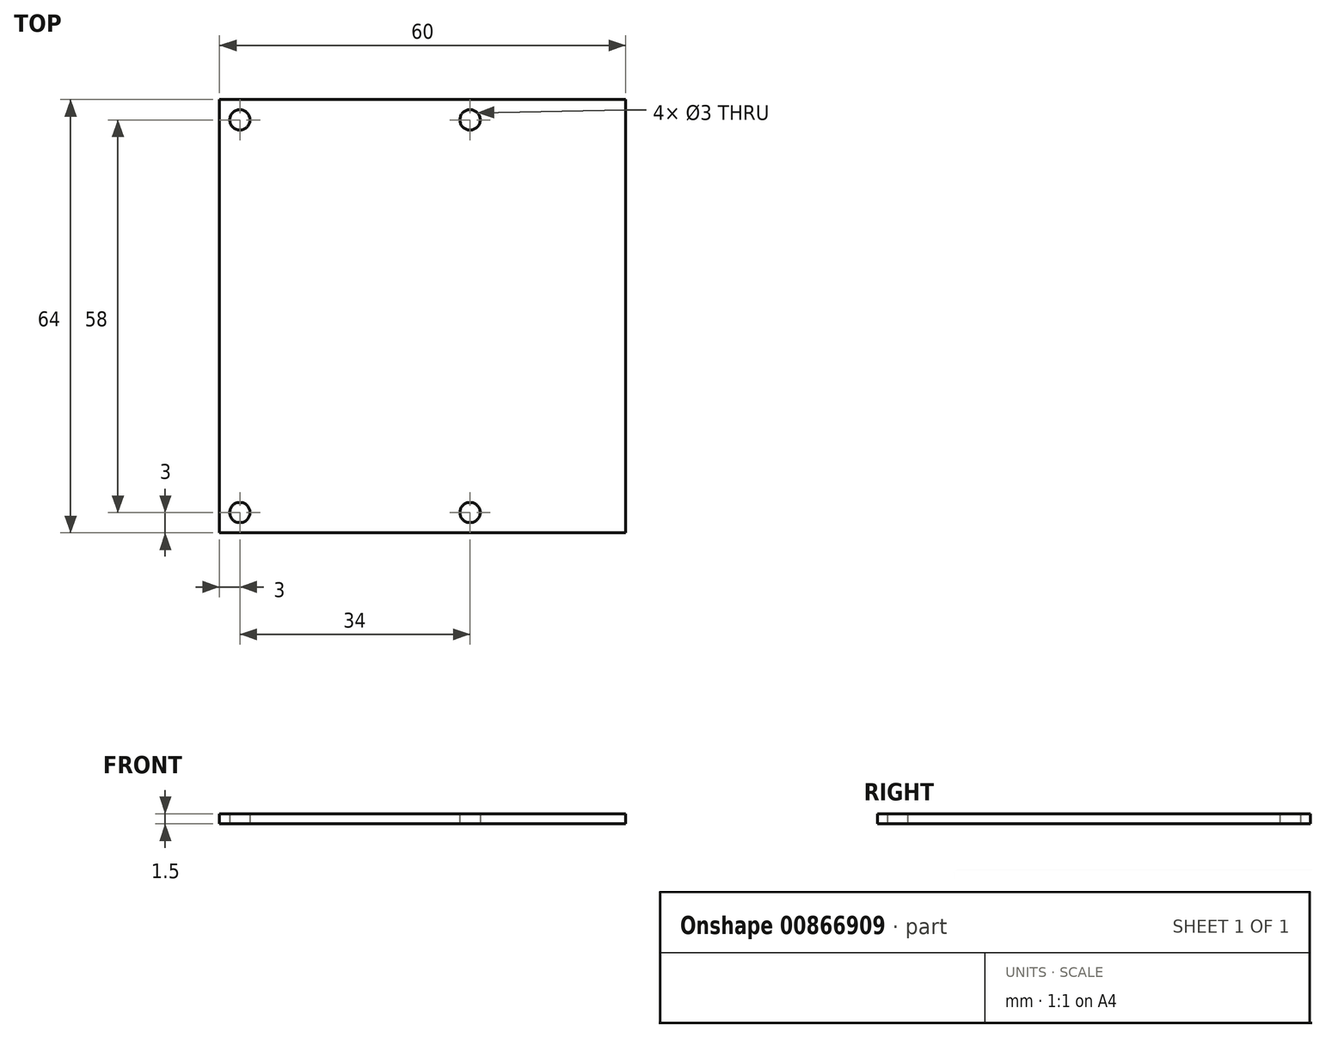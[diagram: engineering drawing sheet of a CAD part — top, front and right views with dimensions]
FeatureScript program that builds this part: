
annotation { "Feature Type Name" : "Feature", "Feature Type Description" : "" }
export const myFeature = defineFeature(function(context is Context, id is Id, definition is map)
    precondition{}
    {
        {
            var Q0;
            Q0=qCreatedBy(makeId("Top.planeOp"),FACE);
            var sketch = newSketch(context, id + "F0", { "sketchPlane" : qUnion([Q0])});
            skLineSegment(sketch, "E0.bottom", {"start": v(30, -32) * mm, "end": v(-30, -32) * mm});
            skLineSegment(sketch, "E0.top", {"start": v(30, 32) * mm, "end": v(-30, 32) * mm});
            skLineSegment(sketch, "E0.left", {"start": v(30, -32) * mm, "end": v(30, 32) * mm});
            skLineSegment(sketch, "E0.right", {"start": v(-30, -32) * mm, "end": v(-30, 32) * mm});
            skPoint(sketch, "E1.middle", {"position": v(0, 0) * mm});
            skCircle(sketch, "E2", {"center": v(7, 29) * mm, "radius": 1.5 * mm});
            skCircle(sketch, "E3", {"center": v(7, -29) * mm, "radius": 1.5 * mm});
            skCircle(sketch, "E4", {"center": v(-27, -29) * mm, "radius": 1.5 * mm});
            skCircle(sketch, "E5", {"center": v(-27, 29) * mm, "radius": 1.5 * mm});
            skLineSegment(sketch, "E6.bottom", {"start": v(7, -29) * mm, "end": v(-27, -29) * mm, "construction": true});
            skLineSegment(sketch, "E6.top", {"start": v(7, 29) * mm, "end": v(-27, 29) * mm, "construction": true});
            skLineSegment(sketch, "E6.left", {"start": v(7, -29) * mm, "end": v(7, 29) * mm, "construction": true});
            skLineSegment(sketch, "E6.right", {"start": v(-27, -29) * mm, "end": v(-27, 29) * mm, "construction": true});
            skPoint(sketch, "E6.middle", {"position": v(-10, 0) * mm});
            skLineSegment(sketch, "E7", {"start": v(-27, 29) * mm, "end": v(-27, 32) * mm, "construction": true});
            skLineSegment(sketch, "E8", {"start": v(-27, 29) * mm, "end": v(-30, 29) * mm, "construction": true});
            skSolve(sketch);
        }
        {
            var Q0;
            Q0=qSketchRegion(id+"F0",true);
            extrude(context, id + "F1", {"entities" : qUnion([Q0]), "depth" : 1.5 * mm, "offsetDistance" : 25 * mm});
        }
    });
